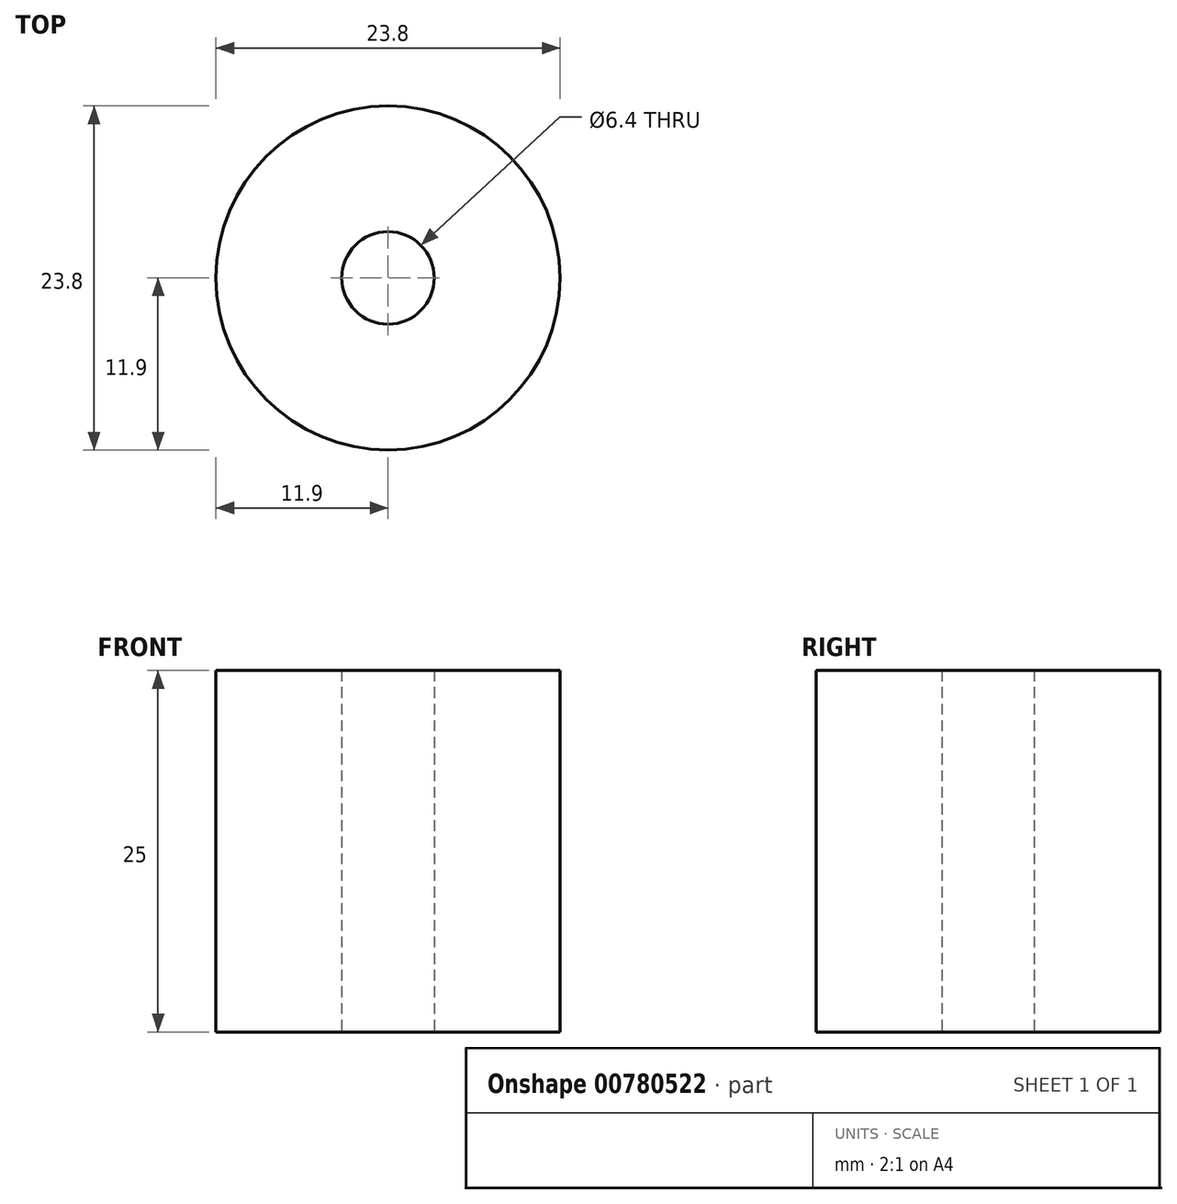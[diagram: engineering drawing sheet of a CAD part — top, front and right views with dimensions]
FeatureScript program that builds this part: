
annotation { "Feature Type Name" : "Feature", "Feature Type Description" : "" }
export const myFeature = defineFeature(function(context is Context, id is Id, definition is map)
    precondition{}
    {
        {
            var Q0;
            Q0=qCreatedBy(makeId("Top.planeOp"),FACE);
            var sketch = newSketch(context, id + "F0", { "sketchPlane" : qUnion([Q0])});
            skCircle(sketch, "E0", {"center": v(0, 0) * mm, "radius": 11.9 * mm});
            skCircle(sketch, "E1", {"center": v(0, 0) * mm, "radius": 3.2 * mm});
            skSolve(sketch);
        }
        {
            var Q0;
            Q0=makeQuery(id+"F0.imprint","IMPRINT",FACE,{"disambiguationData":[TD([[makeQuery(id+"F0.imprint","IMPRINT",EDGE,{"derivedFrom":sQuery(id+"F0.wireOp",EDGE,"E0")}),1.0]])]});
            extrude(context, id + "F1", {"entities" : qUnion([Q0]), "depth" : 25 * mm, "offsetDistance" : 25 * mm});
        }
    });
